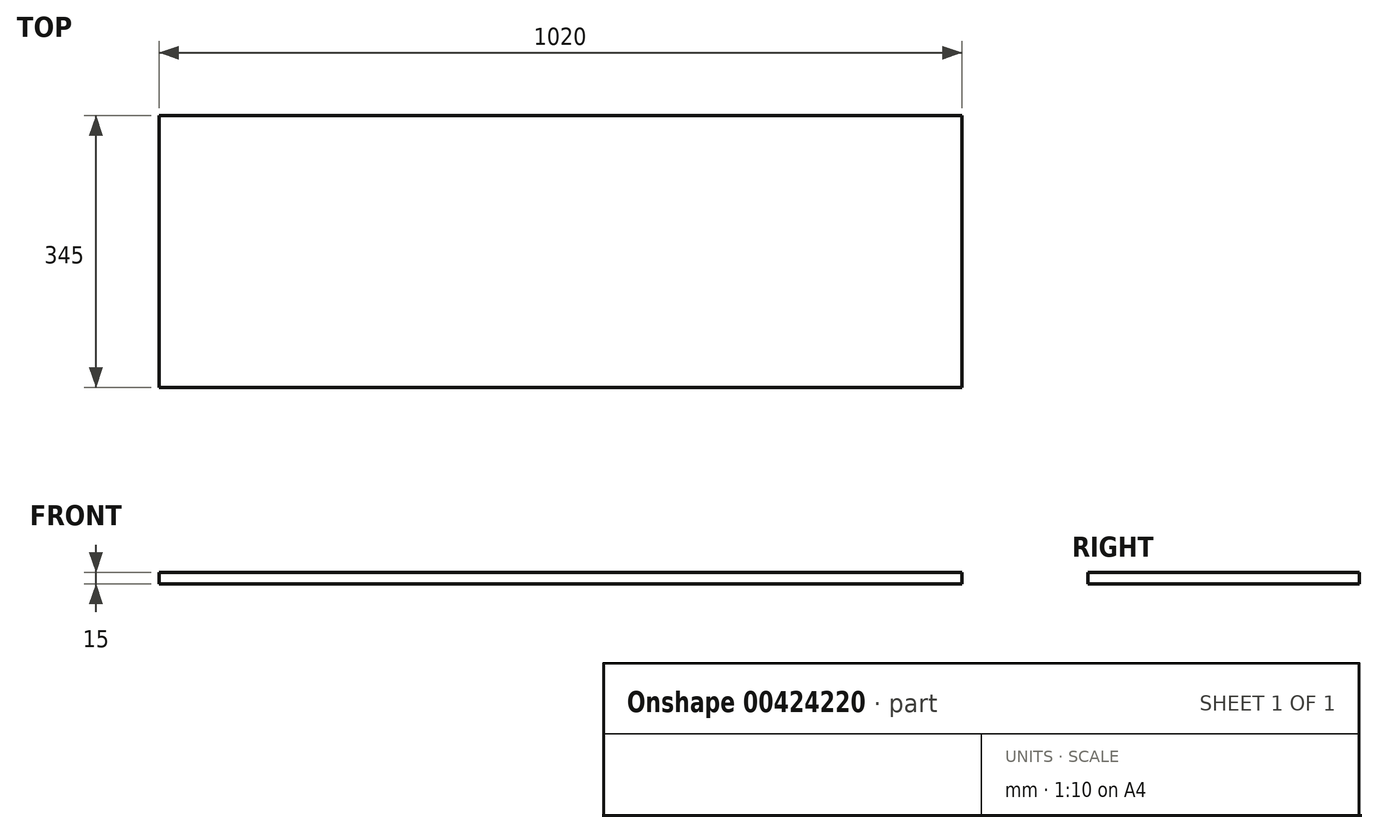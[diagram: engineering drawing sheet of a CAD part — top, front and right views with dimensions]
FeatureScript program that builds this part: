
annotation { "Feature Type Name" : "Feature", "Feature Type Description" : "" }
export const myFeature = defineFeature(function(context is Context, id is Id, definition is map)
    precondition{}
    {
        {
            var Q0;
            Q0=qCreatedBy(makeId("Top.planeOp"),FACE);
            var sketch = newSketch(context, id + "F0", { "sketchPlane" : qUnion([Q0])});
            skLineSegment(sketch, "E0.bottom", {"start": v(-222.47, 179.68) * mm, "end": v(797.53, 179.68) * mm});
            skLineSegment(sketch, "E0.top", {"start": v(-222.47, -165.32) * mm, "end": v(797.53, -165.32) * mm});
            skLineSegment(sketch, "E0.left", {"start": v(-222.47, 179.68) * mm, "end": v(-222.47, -165.32) * mm});
            skLineSegment(sketch, "E0.right", {"start": v(797.53, 179.68) * mm, "end": v(797.53, -165.32) * mm});
            skSolve(sketch);
        }
        {
            var Q0;
            Q0=makeQuery(id+"F0.imprint","IMPRINT",FACE,{"disambiguationData":[TD([[makeQuery(id+"F0.imprint","IMPRINT",EDGE,{"derivedFrom":sQuery(id+"F0.wireOp",EDGE,"E0.bottom")}),-1.0]])]});
            extrude(context, id + "F1", {"entities" : qUnion([Q0]), "depth" : 15 * mm});
        }
    });
